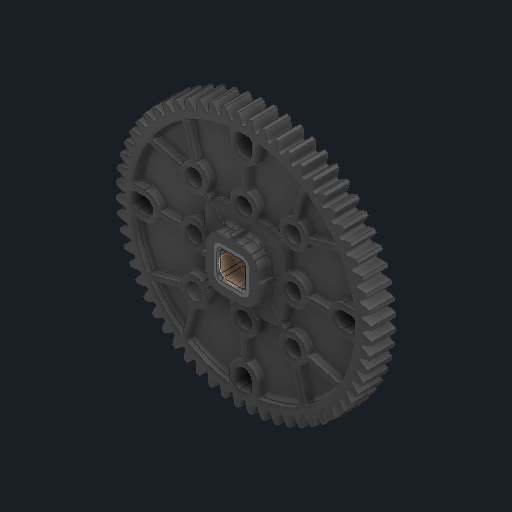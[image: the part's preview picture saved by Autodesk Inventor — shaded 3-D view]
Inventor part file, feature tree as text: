
AUTODESK INVENTOR PART (.ipt)
format: ipt  version: 2025 (Build 290162000, 162)  size: 4,531,712 bytes
history: native  units: in
note: dims shown in document units (in); Inventor stores cm internally (conversion verified against a paired STEP export)
features: other x6, sketch x3
ambient origin geometry x8: Origin, YZ Plane, XZ Plane, XY Plane, X Axis, Y Axis, Z Axis, Center Point
bodies: Solid1 (feature_tree), Solid2 (feature_tree)
feature tree (9):
  other  "Half Cut HS 60T Gear.ipt"
  other  "Solid1::Half Cut HS 60T Gear.ipt"
  other  "Solid2::Half Cut HS 60T Gear.ipt"
  other  "TaggingFeature1"
  sketch  "Sketch1"  dims[d0=0.3937in]
  sketch  "Sketch2"
  sketch  "Sketch3"
  other  "Srf1"
  other  "Srf1::Derived"
